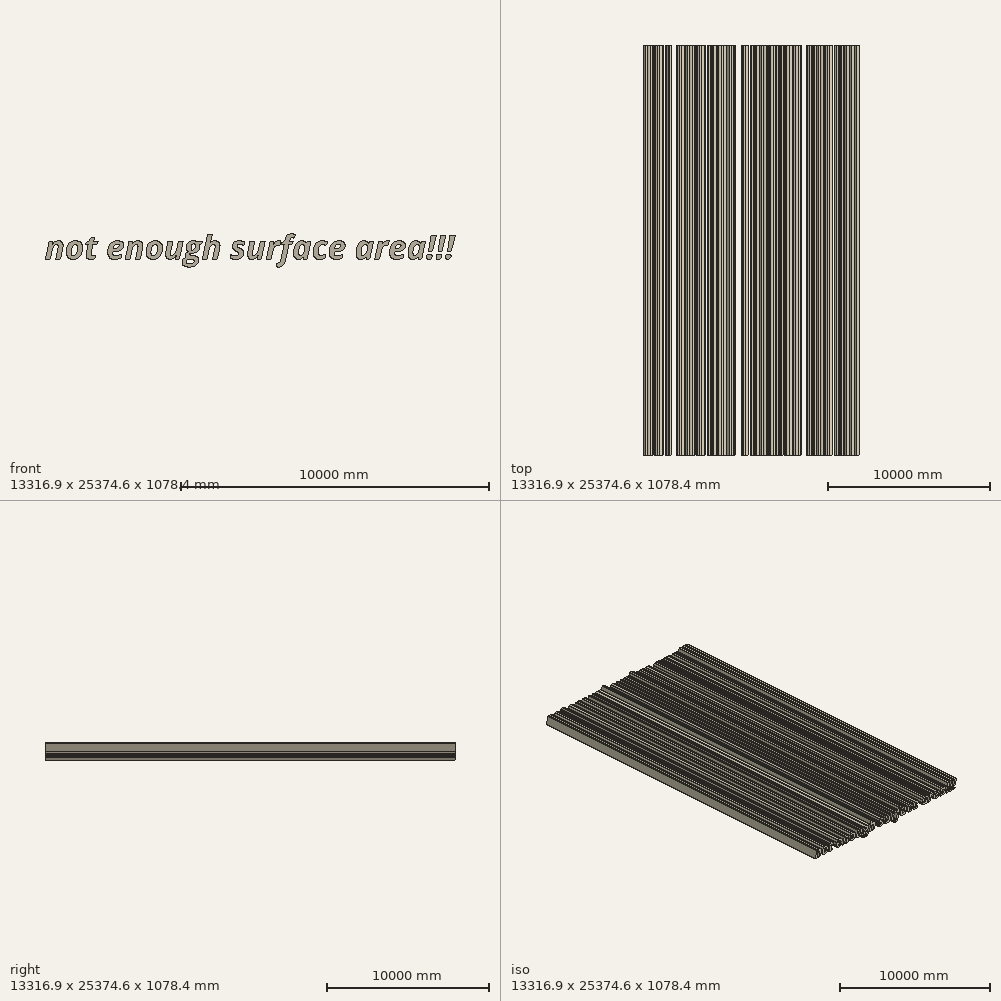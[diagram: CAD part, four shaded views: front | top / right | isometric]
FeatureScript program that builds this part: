
annotation { "Feature Type Name" : "Feature", "Feature Type Description" : "" }
export const myFeature = defineFeature(function(context is Context, id is Id, definition is map)
    precondition{}
    {
        {
            var Q0;
            Q0=qCreatedBy(makeId("Front.planeOp"),FACE);
            var sketch = newSketch(context, id + "F0", { "sketchPlane" : qUnion([Q0])});
            skText(sketch, "E0", { "text": "not enough surface area!!!", "fontName": "OpenSans-BoldItalic.ttf"});
            const initialGuessF0  = {"E0": [-0.1373, -0.14736, 1, 0, 0.77222]};
            skSetInitialGuess(sketch, initialGuessF0);
            skSolve(sketch);
        }
        {
            var Q0;
            Q0 = qSketchRegion(id + "F0", true);
            extrude(context, id + "F1", {"entities" : qUnion([Q0]), "depth" : 25374.6 * mm});
        }
    });
